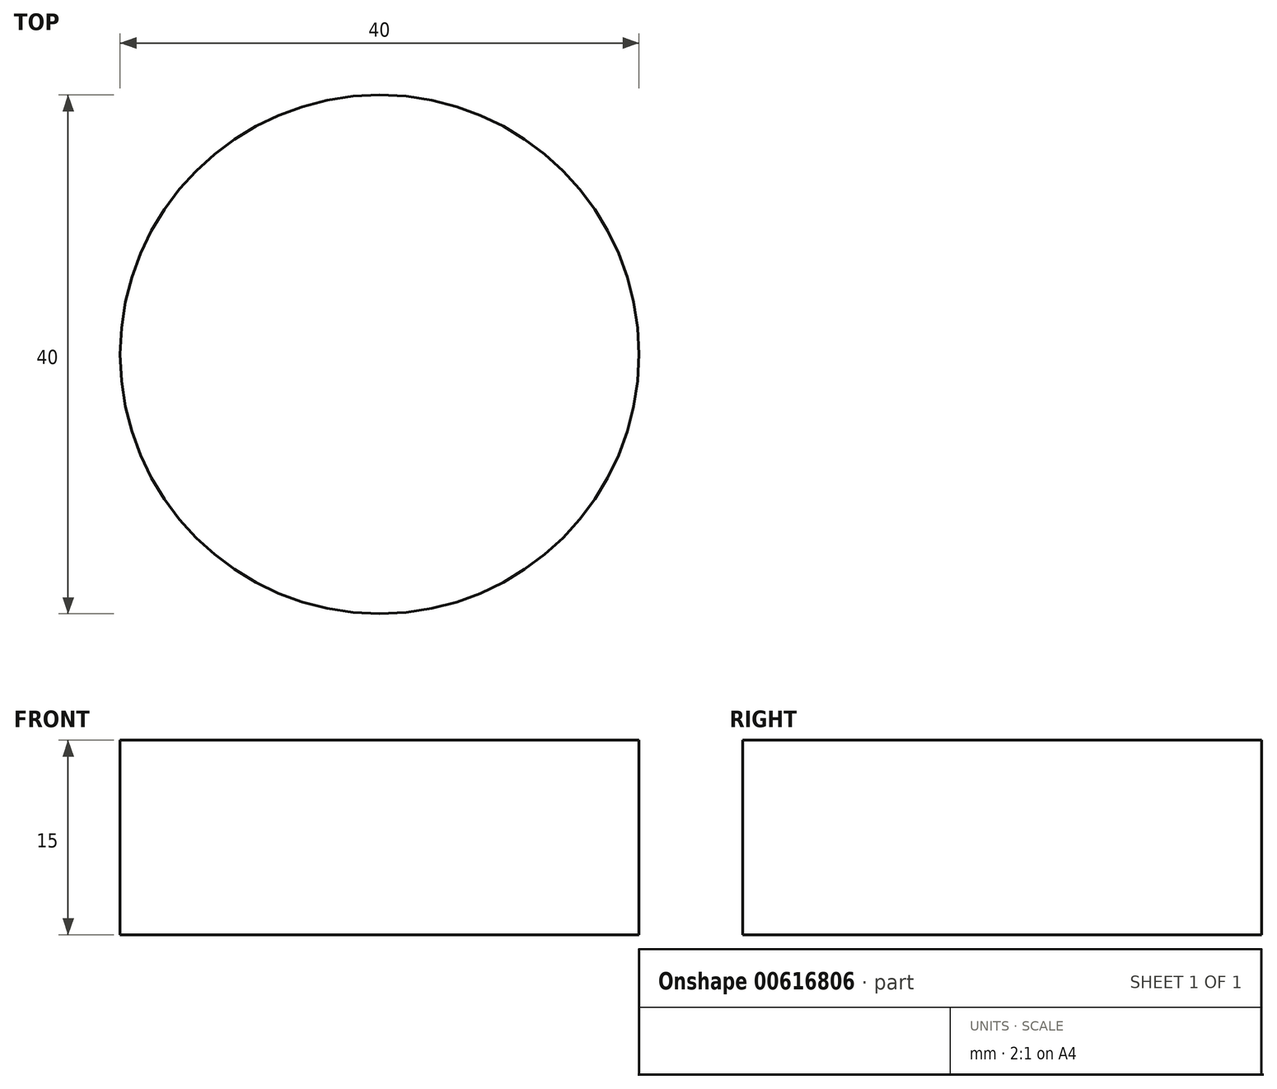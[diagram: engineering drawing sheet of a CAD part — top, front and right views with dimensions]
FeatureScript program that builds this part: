
annotation { "Feature Type Name" : "Feature", "Feature Type Description" : "" }
export const myFeature = defineFeature(function(context is Context, id is Id, definition is map)
    precondition{}
    {
        {
            var Q0;
            Q0=qCreatedBy(makeId("Top.planeOp"),FACE);
            var sketch = newSketch(context, id + "F0", { "sketchPlane" : qUnion([Q0])});
            skCircle(sketch, "E0", {"center": v(0, 0) * mm, "radius": 20 * mm});
            skSolve(sketch);
        }
        {
            var Q0;
            Q0=makeQuery(id+"F0.imprint","IMPRINT",FACE,{"disambiguationData":[TD([[makeQuery(id+"F0.imprint","IMPRINT",EDGE,{"derivedFrom":sQuery(id+"F0.wireOp",EDGE,"E0")}),1.0]])]});
            extrude(context, id + "F1", {"entities" : qUnion([Q0]), "depth" : 15 * mm, "offsetDistance" : 25 * mm});
        }
    });
